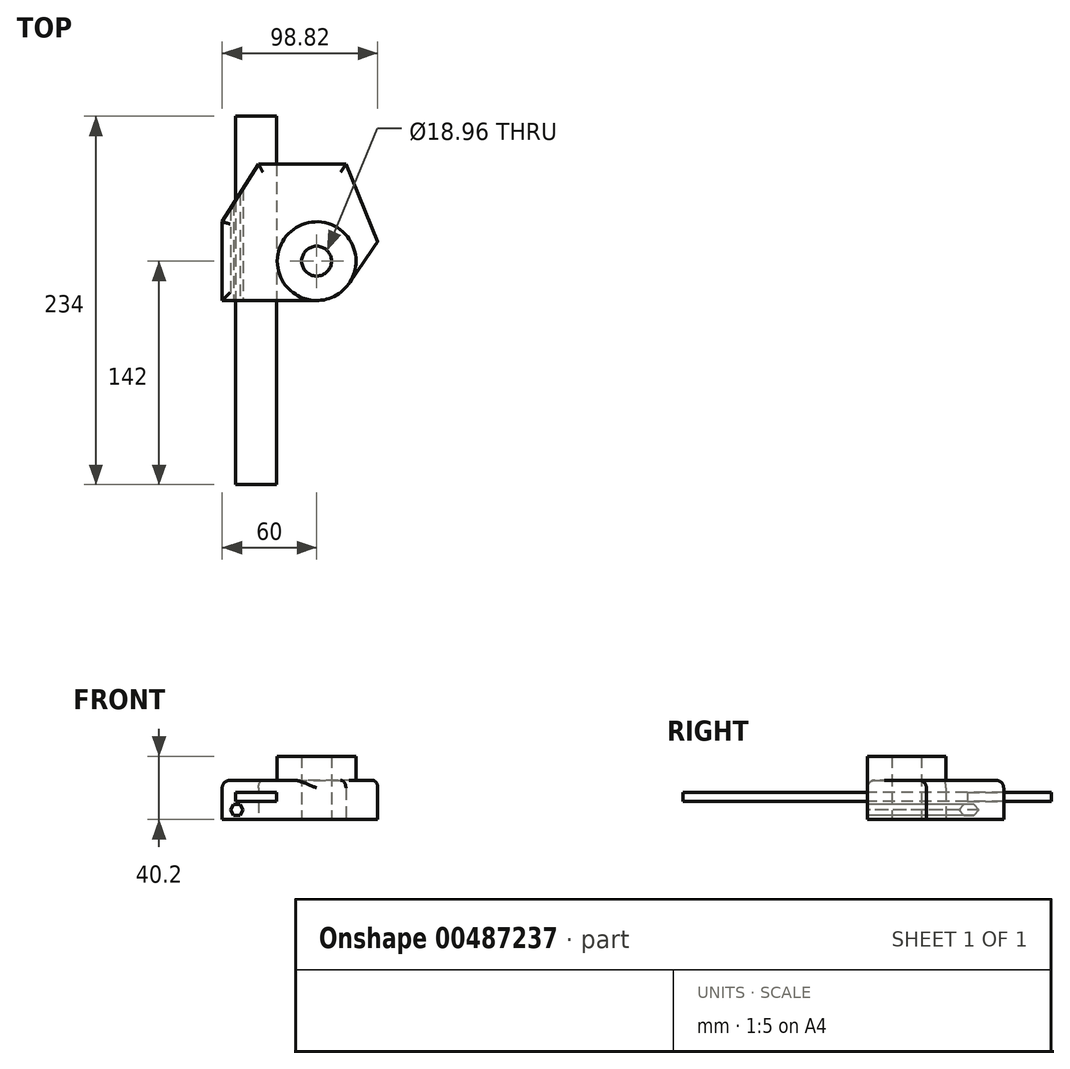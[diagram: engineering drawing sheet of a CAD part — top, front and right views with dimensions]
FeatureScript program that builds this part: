
annotation { "Feature Type Name" : "Feature", "Feature Type Description" : "" }
export const myFeature = defineFeature(function(context is Context, id is Id, definition is map)
    precondition{}
    {
        {
            var Q0;
            Q0=qCreatedBy(makeId("Top.planeOp"),FACE);
            var sketch = newSketch(context, id + "F0", { "sketchPlane" : qUnion([Q0])});
            skLineSegment(sketch, "E0.bottom", {"start": v(30, -25) * mm, "end": v(-30, -25) * mm});
            skLineSegment(sketch, "E0.top", {"start": v(30, 25) * mm, "end": v(-30, 25) * mm});
            skLineSegment(sketch, "E0.left", {"start": v(30, -25) * mm, "end": v(30, 25) * mm});
            skLineSegment(sketch, "E0.right", {"start": v(-30, -25) * mm, "end": v(-30, 25) * mm});
            skPoint(sketch, "E0.middle", {"position": v(0, 0) * mm});
            skCircle(sketch, "E1", {"center": v(30, 0) * mm, "radius": 25 * mm});
            skLineSegment(sketch, "E2", {"start": v(-30, 25) * mm, "end": v(-6.93, 61.64) * mm});
            skLineSegment(sketch, "E3", {"start": v(-6.93, 61.64) * mm, "end": v(48.58, 61.64) * mm});
            skLineSegment(sketch, "E4", {"start": v(48.58, 61.64) * mm, "end": v(68.82, 12.58) * mm});
            skLineSegment(sketch, "E5", {"start": v(68.82, 12.58) * mm, "end": v(50.66, -14.08) * mm});
            skCircle(sketch, "E6", {"center": v(30, 0) * mm, "radius": 9.48 * mm});
            skSolve(sketch);
        }
        {
            var Q0;
            {var subQ0=sQuery(id+"F0.wireOp",EDGE,"E0.bottom");Q0=makeQuery(id+"F0.imprint","IMPRINT",FACE,{"disambiguationData":[TD([[makeQuery(id+"F0.imprint","IMPRINT",EDGE,{"derivedFrom":subQ0}),-1.0]])]});}
            var Q1;
            {var subQ1=sQuery(id+"F0.wireOp",EDGE,"E0.top");Q1=makeQuery(id+"F0.imprint","IMPRINT",FACE,{"disambiguationData":[TD([[makeQuery(id+"F0.imprint","IMPRINT",EDGE,{"derivedFrom":subQ1}),-1.0]])]});}
            var Q2;
            {var subQ1=sQuery(id+"F0.wireOp",EDGE,"E0.left");var subQ4=sQuery(id+"F0.wireOp",EDGE,"E6");var subQ7=makeQuery(id+"F0.imprint","INTERSECT",VERTEX,{"disambiguationData":[OD(0.0)],"derivedFrom":[subQ1,subQ4]});Q2=makeQuery(id+"F0.imprint","IMPRINT",FACE,{"disambiguationData":[TD([[makeQuery(id+"F0.imprint","IMPRINT",EDGE,{"disambiguationData":[TD([[subQ7,-1.0]])],"derivedFrom":subQ4}),-1.0]])]});}
            var Q3;
            {var subQ1=sQuery(id+"F0.wireOp",EDGE,"E0.left");var subQ3=sQuery(id+"F0.wireOp",EDGE,"E6");var subQ4=makeQuery(id+"F0.imprint","INTERSECT",VERTEX,{"disambiguationData":[OD(0.0)],"derivedFrom":[subQ1,subQ3]});Q3=makeQuery(id+"F0.imprint","IMPRINT",FACE,{"disambiguationData":[TD([[makeQuery(id+"F0.imprint","IMPRINT",EDGE,{"disambiguationData":[TD([[subQ4,1.0]])],"derivedFrom":subQ3}),-1.0]])]});}
            extrude(context, id + "F1", {"entities" : qUnion([Q0, Q1, Q2, Q3]), "depth" : 25 * mm, "offsetDistance" : 25 * mm});
        }
        {
            var Q0;
            {var subQ0=sQuery(id+"F0.wireOp",EDGE,"E6");var subQ1=sQuery(id+"F0.wireOp",EDGE,"E0.left");var subQ2=makeQuery(id+"F0.imprint","INTERSECT",VERTEX,{"disambiguationData":[OD(0.0)],"derivedFrom":[subQ1,subQ0]});Q0=makeQuery(id+"F0.imprint","IMPRINT",FACE,{"disambiguationData":[TD([[makeQuery(id+"F0.imprint","IMPRINT",EDGE,{"disambiguationData":[TD([[subQ2,-1.0]])],"derivedFrom":subQ1}),-1.0]])]});}
            var Q1;
            {var subQ0=sQuery(id+"F0.wireOp",EDGE,"E6");var subQ1=sQuery(id+"F0.wireOp",EDGE,"E0.left");var subQ2=makeQuery(id+"F0.imprint","INTERSECT",VERTEX,{"disambiguationData":[OD(0.0)],"derivedFrom":[subQ1,subQ0]});Q1=makeQuery(id+"F0.imprint","IMPRINT",FACE,{"disambiguationData":[TD([[makeQuery(id+"F0.imprint","IMPRINT",EDGE,{"disambiguationData":[TD([[subQ2,-1.0]])],"derivedFrom":subQ1}),1.0]])]});}
            extrude(context, id + "F2", {"entities" : qUnion([Q0, Q1]), "operationType" : NewBodyOperationType.ADD, "depth" : 40.2 * mm, "offsetDistance" : 25 * mm});
        }
        {
            var Q0;
            Q0=makeQuery(id+"F1.opExtrude","CAP_EDGE",EDGE,{"disambiguationData":[OSD([sQuery(id+"F0.wireOp",EDGE,"E0.bottom")])],"isStart":false});
            var Q1;
            Q1=makeQuery(id+"F1.opExtrude","CAP_EDGE",EDGE,{"disambiguationData":[OSD([sQuery(id+"F0.wireOp",EDGE,"E0.right")])],"isStart":false});
            var Q2;
            Q2=makeQuery(id+"F1.opExtrude","CAP_EDGE",EDGE,{"disambiguationData":[OSD([sQuery(id+"F0.wireOp",EDGE,"E2")])],"isStart":false});
            var Q3;
            Q3=makeQuery(id+"F1.opExtrude","CAP_EDGE",EDGE,{"disambiguationData":[OSD([sQuery(id+"F0.wireOp",EDGE,"E3")])],"isStart":false});
            var Q4;
            Q4=makeQuery(id+"F1.opExtrude","CAP_EDGE",EDGE,{"disambiguationData":[OSD([sQuery(id+"F0.wireOp",EDGE,"E4")])],"isStart":false});
            var Q5;
            Q5=makeQuery(id+"F1.opExtrude","CAP_EDGE",EDGE,{"disambiguationData":[OSD([sQuery(id+"F0.wireOp",EDGE,"E6")])],"isStart":false});
            fillet(context, id + "F3", {"entities" : qUnion([Q0, Q1, Q2, Q3, Q4, Q5]), "radius" : 5 * mm, "tangentPropagation" : true, "allowEdgeOverflow" : false});
        }
        {
            var Q0;
            Q0=makeQuery(id+"F1.opExtrude","SWEPT_FACE",FACE,{"disambiguationData":[OSD([sQuery(id+"F0.wireOp",EDGE,"E0.bottom")])]});
            var sketch = newSketch(context, id + "F4", { "sketchPlane" : qUnion([Q0])});
            skLineSegment(sketch, "E7.bottom", {"start": v(4.55, 11.62) * mm, "end": v(-21.45, 11.62) * mm});
            skLineSegment(sketch, "E7.top", {"start": v(4.55, 17.26) * mm, "end": v(-21.45, 17.26) * mm});
            skLineSegment(sketch, "E7.left", {"start": v(4.55, 11.62) * mm, "end": v(4.55, 17.26) * mm});
            skLineSegment(sketch, "E7.right", {"start": v(-21.45, 11.62) * mm, "end": v(-21.45, 17.26) * mm});
            skPoint(sketch, "E7.middle", {"position": v(-8.45, 14.44) * mm});
            skCircle(sketch, "E8.cCircle", {"center": v(-20.8, 6.2) * mm, "radius": 3.47 * mm, "construction": true});
            skLineSegment(sketch, "E8.0", {"start": v(-18.8, 2.74) * mm, "end": v(-22.8, 2.74) * mm});
            skLineSegment(sketch, "E8.1", {"start": v(-22.8, 2.74) * mm, "end": v(-24.8, 6.2) * mm});
            skLineSegment(sketch, "E8.2", {"start": v(-24.8, 6.2) * mm, "end": v(-22.8, 9.68) * mm});
            skLineSegment(sketch, "E8.3", {"start": v(-22.8, 9.68) * mm, "end": v(-18.8, 9.68) * mm});
            skLineSegment(sketch, "E8.4", {"start": v(-18.8, 9.68) * mm, "end": v(-16.8, 6.2) * mm});
            skLineSegment(sketch, "E8.5", {"start": v(-16.8, 6.2) * mm, "end": v(-18.8, 2.74) * mm});
            skPoint(sketch, "E8.0.midPoint", {"position": v(-20.8, 2.74) * mm});
            skCircle(sketch, "E9.1.0.0", {"center": v(-5.8, 6.2) * mm, "radius": 3.47 * mm, "construction": true});
            skCircle(sketch, "E9.2.0.0", {"center": v(9.2, 6.2) * mm, "radius": 3.47 * mm, "construction": true});
            skCircle(sketch, "E9.3.0.0", {"center": v(24.2, 6.2) * mm, "radius": 3.47 * mm, "construction": true});
            skLineSegment(sketch, "E9.direction1", {"start": v(-20.8, 6.2) * mm, "end": v(-5.8, 6.2) * mm, "construction": true});
            skSolve(sketch);
        }
        {
            var Q0;
            Q0=makeQuery(id+"F4.imprint","IMPRINT",FACE,{"disambiguationData":[TD([[makeQuery(id+"F4.imprint","IMPRINT",EDGE,{"derivedFrom":sQuery(id+"F4.wireOp",EDGE,"E8.0")}),-1.0]])]});
            var Q1;
            Q1=makeQuery(id+"F4.imprint","IMPRINT",FACE,{"disambiguationData":[TD([[makeQuery(id+"F4.imprint","IMPRINT",EDGE,{"derivedFrom":sQuery(id+"F4.wireOp",EDGE,"E7.bottom")}),-1.0]])]});
            extrude(context, id + "F5", {"entities" : qUnion([Q0, Q1]), "operationType" : NewBodyOperationType.REMOVE, "endBound" : BoundingType.THROUGH_ALL, "oppositeDirection" : true, "depth" : 25 * mm, "offsetDistance" : 25 * mm});
        }
        {
            var Q0;
            Q0=makeQuery(id+"F4.imprint","IMPRINT",FACE,{"disambiguationData":[TD([[makeQuery(id+"F4.imprint","IMPRINT",EDGE,{"derivedFrom":sQuery(id+"F4.wireOp",EDGE,"E7.bottom")}),-1.0]])]});
            extrude(context, id + "F6", {"entities" : qUnion([Q0]), "endBound" : BoundingType.SYMMETRIC, "depth" : 234 * mm, "offsetDistance" : 25 * mm});
        }
    });
